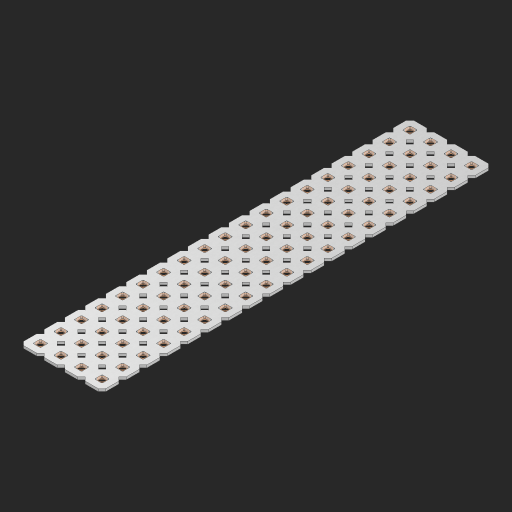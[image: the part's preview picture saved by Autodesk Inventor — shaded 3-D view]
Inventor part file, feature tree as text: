
AUTODESK INVENTOR PART (.ipt)
format: ipt  version: 2023 (Build 270158000, 158)  size: 1,159,680 bytes
history: native  units: in
note: dims shown in document units (in); Inventor stores cm internally (conversion verified against a paired STEP export)
features: other x77, extrude x75, sketch x2, pattern_linear x1
ambient origin geometry x8: Origin, YZ Plane, XZ Plane, XY Plane, X Axis, Y Axis, Z Axis, Center Point
bodies: Solid1 (feature_tree), Body (feature_tree)
feature tree (155):
  pattern_linear  "Rectangular Pattern1"  Spacing1=0.09in  [1 undecoded]
  sketch  "Sketch1"  dims[d1=0.5in]
  sketch  "Sketch2"  dims[d2=0.182in d3=0.09in d4=0.09in d5=0.09in d6=0.09in d7=0.09in d8=0.09in d9=0.09in d10=0.09in d11=0.02in d13=0.0in d14=0.172in d15=0.0625in d16=0.0in d19=0.5in d22=0.5in]
  other  "Srf1"
  other  "Srf126"
  other  "Srf127"
  other  "Srf128"
  other  "Srf129"
  other  "Srf130"
  other  "Srf131"
  other  "Srf250"
  other  "Srf251"
  other  "Srf252"
  other  "Srf253"
  other  "Srf254"
  other  "Srf255"
  other  "Srf256"
  other  "Srf257"
  other  "Srf258"
  other  "Srf259"
  other  "Srf260"
  other  "Srf261"
  other  "Srf268"
  other  "Srf269"
  other  "Srf270"
  other  "Srf271"
  other  "Srf272"
  other  "Srf273"
  other  "Srf274"
  other  "Srf275"
  other  "Srf276"
  other  "Srf277"
  other  "Srf278"
  other  "Srf279"
  other  "Srf280"
  other  "Srf281"
  other  "Srf282"
  other  "Srf283"
  other  "Srf284"
  other  "Srf285"
  other  "Srf286"
  other  "Srf293"
  other  "Srf294"
  other  "Srf295"
  other  "Srf296"
  other  "Srf297"
  other  "Srf298"
  other  "Srf299"
  other  "Srf300"
  other  "Srf301"
  other  "Srf302"
  other  "Srf303"
  other  "Srf304"
  other  "Srf305"
  other  "Srf306"
  other  "Srf307"
  other  "Srf308"
  other  "Srf309"
  other  "Srf310"
  other  "Srf311"
  other  "Srf318"
  other  "Srf319"
  other  "Srf320"
  other  "Srf321"
  other  "Srf322"
  other  "Srf323"
  other  "Srf324"
  other  "Srf325"
  other  "Srf326"
  other  "Srf327"
  other  "Srf328"
  other  "Srf329"
  other  "Srf330"
  other  "Srf331"
  other  "Srf332"
  other  "Srf333"
  other  "Srf334"
  other  "Srf335"
  other  "Srf336"
  other  "Circle"
  extrude  "ExtrusionSrf126"  Depth=0.09in
  extrude  "ExtrusionSrf127"  Depth=0.09in
  extrude  "ExtrusionSrf128"  Depth=0.09in
  extrude  "ExtrusionSrf129"  Depth=0.09in
  extrude  "ExtrusionSrf130"  Depth=0.09in
  extrude  "ExtrusionSrf131"  Depth=0.09in
  extrude  "ExtrusionSrf250"  Depth=0.09in
  extrude  "ExtrusionSrf251"  Depth=0.02in
  extrude  "ExtrusionSrf252"  TaperAngle=0.0deg  [1 undecoded]
  extrude  "ExtrusionSrf253"  Depth=0.5in
  extrude  "ExtrusionSrf254"  Depth=0.0625in TaperAngle=0.0deg
  extrude  "ExtrusionSrf255"  Depth=0.5in
  extrude  "ExtrusionSrf256"  Depth=0.5in
  extrude  "ExtrusionSrf257"  [1 undecoded]
  extrude  "ExtrusionSrf258"  [1 undecoded]
  extrude  "ExtrusionSrf259"  [1 undecoded]
  extrude  "ExtrusionSrf260"  [1 undecoded]
  extrude  "ExtrusionSrf261"  [1 undecoded]
  extrude  "ExtrusionSrf268"  [1 undecoded]
  extrude  "ExtrusionSrf269"  [1 undecoded]
  extrude  "ExtrusionSrf270"  [1 undecoded]
  extrude  "ExtrusionSrf271"  [1 undecoded]
  extrude  "ExtrusionSrf272"  [1 undecoded]
  extrude  "ExtrusionSrf273"  [1 undecoded]
  extrude  "ExtrusionSrf274"  [1 undecoded]
  extrude  "ExtrusionSrf275"  [1 undecoded]
  extrude  "ExtrusionSrf276"  [1 undecoded]
  extrude  "ExtrusionSrf277"  [1 undecoded]
  extrude  "ExtrusionSrf278"  [1 undecoded]
  extrude  "ExtrusionSrf279"  [1 undecoded]
  extrude  "ExtrusionSrf280"  [1 undecoded]
  extrude  "ExtrusionSrf281"  [1 undecoded]
  extrude  "ExtrusionSrf282"  [1 undecoded]
  extrude  "ExtrusionSrf283"  [1 undecoded]
  extrude  "ExtrusionSrf284"  [1 undecoded]
  extrude  "ExtrusionSrf285"  [1 undecoded]
  extrude  "ExtrusionSrf286"  [1 undecoded]
  extrude  "ExtrusionSrf293"  [1 undecoded]
  extrude  "ExtrusionSrf294"  [1 undecoded]
  extrude  "ExtrusionSrf295"  [1 undecoded]
  extrude  "ExtrusionSrf296"  [1 undecoded]
  extrude  "ExtrusionSrf297"  [1 undecoded]
  extrude  "ExtrusionSrf298"  [1 undecoded]
  extrude  "ExtrusionSrf299"  [1 undecoded]
  extrude  "ExtrusionSrf300"  [1 undecoded]
  extrude  "ExtrusionSrf301"  [1 undecoded]
  extrude  "ExtrusionSrf302"  [1 undecoded]
  extrude  "ExtrusionSrf303"  [1 undecoded]
  extrude  "ExtrusionSrf304"  [1 undecoded]
  extrude  "ExtrusionSrf305"  [1 undecoded]
  extrude  "ExtrusionSrf306"  [1 undecoded]
  extrude  "ExtrusionSrf307"  [1 undecoded]
  extrude  "ExtrusionSrf308"  [1 undecoded]
  extrude  "ExtrusionSrf309"  [1 undecoded]
  extrude  "ExtrusionSrf310"  [1 undecoded]
  extrude  "ExtrusionSrf311"  [1 undecoded]
  extrude  "ExtrusionSrf318"  [1 undecoded]
  extrude  "ExtrusionSrf319"  [1 undecoded]
  extrude  "ExtrusionSrf320"  [1 undecoded]
  extrude  "ExtrusionSrf321"  [1 undecoded]
  extrude  "ExtrusionSrf322"  [1 undecoded]
  extrude  "ExtrusionSrf323"  [1 undecoded]
  extrude  "ExtrusionSrf324"  [1 undecoded]
  extrude  "ExtrusionSrf325"  [1 undecoded]
  extrude  "ExtrusionSrf326"  [1 undecoded]
  extrude  "ExtrusionSrf327"  [1 undecoded]
  extrude  "ExtrusionSrf328"  [1 undecoded]
  extrude  "ExtrusionSrf329"  [1 undecoded]
  extrude  "ExtrusionSrf330"  [1 undecoded]
  extrude  "ExtrusionSrf331"  [1 undecoded]
  extrude  "ExtrusionSrf332"  [1 undecoded]
  extrude  "ExtrusionSrf333"  [1 undecoded]
  extrude  "ExtrusionSrf334"  [1 undecoded]
  extrude  "ExtrusionSrf335"  [1 undecoded]
  extrude  "ExtrusionSrf336"  [1 undecoded]
note: 64 required parameter values undecoded (feature->parameter linkage not recoverable at this tier; creation-order binding heuristic only, values carry confidence <= 0.55)
